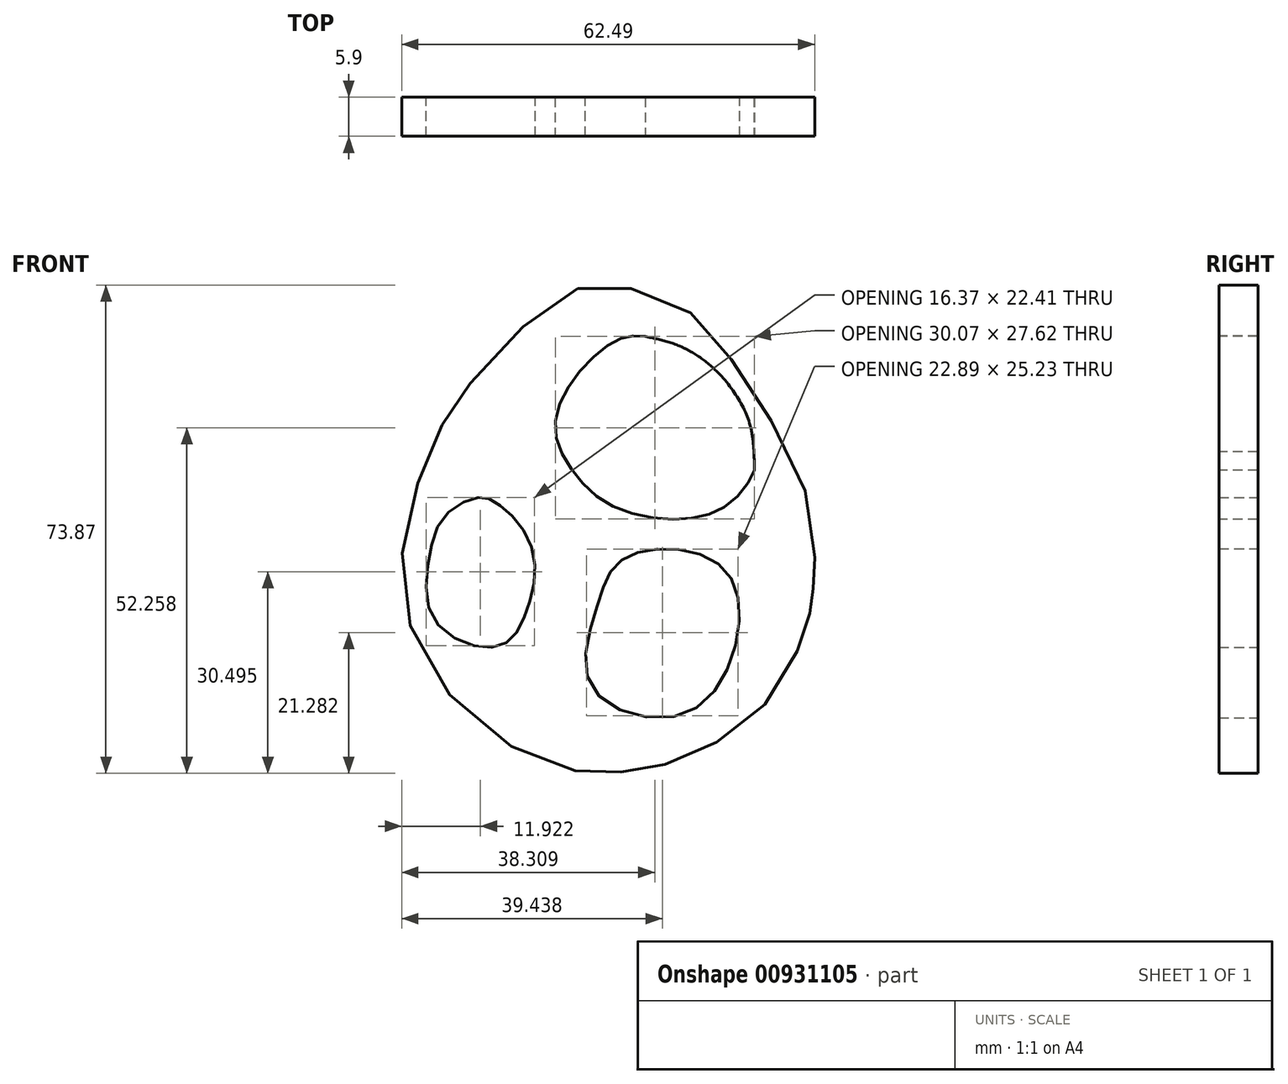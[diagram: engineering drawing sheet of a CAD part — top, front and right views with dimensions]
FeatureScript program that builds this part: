
annotation { "Feature Type Name" : "Feature", "Feature Type Description" : "" }
export const myFeature = defineFeature(function(context is Context, id is Id, definition is map)
    precondition{}
    {
        {
            var Q0;
            Q0=qCreatedBy(makeId("Front.planeOp"),FACE);
            var sketch = newSketch(context, id + "F0", { "sketchPlane" : qUnion([Q0])});
            skFitSpline(sketch, "E0", {"points": [v(-52.1, 58.79) * mm, v(-56.55, 52.03) * mm, v(-61.35, 38.98) * mm, v(-61.35, 22.67) * mm, v(-49.75, 6.36) * mm, v(-35.6, 0) * mm, v(-29.2, 0) * mm, v(-22.98, 1.01) * mm, v(-13.7, 5.12) * mm, v(-5.01, 13.44) * mm, v(-1.19, 22.33) * mm, v(-0.6, 24.43) * mm, v(-0.29, 26.58) * mm, v(-0.17, 28.24) * mm, v(0, 30.62) * mm, v(-1.64, 43.25) * mm, v(-10.77, 59.54) * mm, v(-18.74, 69.4) * mm, v(-30.67, 73.55) * mm, v(-38.87, 71.57) * mm, v(-52.1, 58.79) * mm]});
            skSolve(sketch);
        }
        {
            var Q0;
            Q0=makeQuery(id+"F0.imprint","IMPRINT",FACE,{"disambiguationData":[TD([[makeQuery(id+"F0.imprint","IMPRINT",EDGE,{"derivedFrom":sQuery(id+"F0.wireOp",EDGE,"E0")}),1.0]])]});
            extrude(context, id + "F1", {"entities" : qUnion([Q0]), "depth" : 5.9 * mm, "offsetDistance" : 25.4 * mm});
        }
        {
            var Q0;
            Q0=makeQuery(id+"F1.opExtrude","CAP_FACE",FACE,{"disambiguationData":[OSD([sQuery(id+"F0.wireOp",EDGE,"E0")])],"isStart":false});
            var sketch = newSketch(context, id + "F2", { "sketchPlane" : qUnion([Q0])});
            skFitSpline(sketch, "E1", {"points": [v(-25.61, 65.84) * mm, v(-20.41, 64.4) * mm, v(-14.32, 60.1) * mm, v(-9.84, 52.76) * mm, v(-9.13, 45.59) * mm], "startDerivative": vector(23.65, -4.67) * mm, "endDerivative": vector(-0.08, -28.44) * mm});
            skFitSpline(sketch, "E2", {"points": [v(-25.61, 65.84) * mm, v(-29.37, 65.5) * mm, v(-35.47, 60.64) * mm, v(-39.23, 52.76) * mm, v(-36.9, 45.95) * mm, v(-30.27, 40.03) * mm, v(-20.06, 38.24) * mm, v(-12.89, 40.57) * mm, v(-9.13, 45.59) * mm, v(-9.12, 47.97) * mm, v(-9.84, 52.76) * mm, v(-14.32, 60.1) * mm, v(-20.41, 64.4) * mm, v(-25.61, 65.84) * mm]});
            skSolve(sketch);
        }
        {
            var Q0;
            {var subQ0=sQuery(id+"F2.wireOp",EDGE,"E2");var subQ1=sQuery(id+"F2.wireOp",EDGE,"E1");var subQ2=makeQuery(id+"F2.imprint","INTERSECT",VERTEX,{"disambiguationData":[OD(0.0)],"derivedFrom":[subQ1,subQ0]});Q0=makeQuery(id+"F2.imprint","IMPRINT",FACE,{"disambiguationData":[TD([[makeQuery(id+"F2.imprint","IMPRINT",EDGE,{"disambiguationData":[TD([[subQ2,-1.0]])],"derivedFrom":subQ1}),-1.0]])]});}
            extrude(context, id + "F3", {"entities" : qUnion([Q0]), "operationType" : NewBodyOperationType.REMOVE, "oppositeDirection" : true, "depth" : 25 * mm, "offsetDistance" : 25 * mm});
        }
        {
            var Q0;
            Q0=makeQuery(id+"F1.opExtrude","CAP_FACE",FACE,{"disambiguationData":[OSD([sQuery(id+"F0.wireOp",EDGE,"E0")])],"isStart":false});
            var sketch = newSketch(context, id + "F4", { "sketchPlane" : qUnion([Q0])});
            skFitSpline(sketch, "E3", {"points": [v(-50.88, 41.47) * mm, v(-48.55, 40.93) * mm, v(-44.6, 37.35) * mm, v(-42.28, 31.07) * mm, v(-43.53, 24.44) * mm, v(-46.04, 19.96) * mm, v(-50.7, 18.89) * mm, v(-57.69, 23.19) * mm, v(-58.4, 31.8) * mm, v(-55.9, 38.78) * mm, v(-50.88, 41.47) * mm]});
            skSolve(sketch);
        }
        {
            var Q0;
            Q0=makeQuery(id+"F4.imprint","IMPRINT",FACE,{"disambiguationData":[TD([[makeQuery(id+"F4.imprint","IMPRINT",EDGE,{"derivedFrom":sQuery(id+"F4.wireOp",EDGE,"E3")}),-1.0]])]});
            extrude(context, id + "F5", {"entities" : qUnion([Q0]), "operationType" : NewBodyOperationType.REMOVE, "oppositeDirection" : true, "depth" : 25 * mm, "offsetDistance" : 25 * mm});
        }
        {
            var Q0;
            Q0=makeQuery(id+"F1.opExtrude","CAP_FACE",FACE,{"disambiguationData":[OSD([sQuery(id+"F0.wireOp",EDGE,"E0")])],"isStart":false});
            var sketch = newSketch(context, id + "F6", { "sketchPlane" : qUnion([Q0])});
            skFitSpline(sketch, "E4", {"points": [v(-32.9, 24.97) * mm, v(-29.73, 31.58) * mm, v(-21.8, 33.7) * mm, v(-13.08, 30) * mm, v(-12.02, 18.9) * mm, v(-20.22, 8.59) * mm, v(-33.7, 12.82) * mm, v(-32.9, 24.97) * mm]});
            skSolve(sketch);
        }
        {
            var Q0;
            Q0=makeQuery(id+"F6.imprint","IMPRINT",FACE,{"disambiguationData":[TD([[makeQuery(id+"F6.imprint","IMPRINT",EDGE,{"derivedFrom":sQuery(id+"F6.wireOp",EDGE,"E4")}),-1.0]])]});
            extrude(context, id + "F7", {"entities" : qUnion([Q0]), "operationType" : NewBodyOperationType.REMOVE, "oppositeDirection" : true, "depth" : 25 * mm, "offsetDistance" : 25 * mm});
        }
    });
